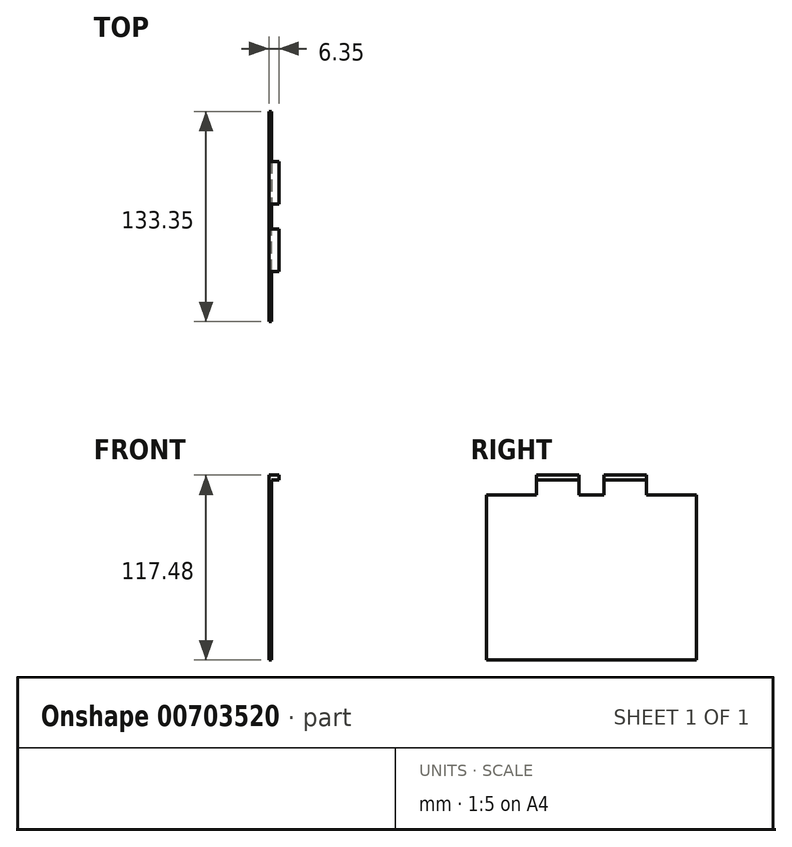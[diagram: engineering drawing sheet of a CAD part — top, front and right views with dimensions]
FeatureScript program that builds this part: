
annotation { "Feature Type Name" : "Feature", "Feature Type Description" : "" }
export const myFeature = defineFeature(function(context is Context, id is Id, definition is map)
    precondition{}
    {
        {
            var Q0;
            Q0=qCreatedBy(makeId("Front.planeOp"),FACE);
            var sketch = newSketch(context, id + "F0", { "sketchPlane" : qUnion([Q0])});
            skLineSegment(sketch, "E0.bottom", {"start": v(-4.86, 82.67) * mm, "end": v(-3.27, 82.67) * mm});
            skLineSegment(sketch, "E0.top", {"start": v(-4.86, -18.93) * mm, "end": v(-3.27, -18.93) * mm});
            skLineSegment(sketch, "E0.left", {"start": v(-4.86, 82.67) * mm, "end": v(-4.86, -18.93) * mm});
            skLineSegment(sketch, "E0.right", {"start": v(-3.27, 82.67) * mm, "end": v(-3.27, -18.93) * mm});
            skLineSegment(sketch, "E1.bottom", {"start": v(-4.86, 95.37) * mm, "end": v(-3.27, 95.37) * mm});
            skLineSegment(sketch, "E1.left", {"start": v(-4.86, 95.37) * mm, "end": v(-4.86, 82.67) * mm});
            skLineSegment(sketch, "E1.right", {"start": v(-3.27, 95.37) * mm, "end": v(-3.27, 82.67) * mm});
            skLineSegment(sketch, "E2.bottom", {"start": v(-4.86, 95.37) * mm, "end": v(1.5, 95.37) * mm});
            skLineSegment(sketch, "E2.top", {"start": v(-4.86, 98.55) * mm, "end": v(1.5, 98.55) * mm});
            skLineSegment(sketch, "E2.left", {"start": v(-4.86, 95.37) * mm, "end": v(-4.86, 98.55) * mm});
            skLineSegment(sketch, "E2.right", {"start": v(1.5, 95.37) * mm, "end": v(1.5, 98.55) * mm});
            skLineSegment(sketch, "E3.bottom", {"start": v(1.5, 95.37) * mm, "end": v(-0.1, 95.37) * mm});
            skLineSegment(sketch, "E3.top", {"start": v(1.5, 89.02) * mm, "end": v(-0.1, 89.02) * mm});
            skLineSegment(sketch, "E3.left", {"start": v(1.5, 95.37) * mm, "end": v(1.5, 89.02) * mm});
            skLineSegment(sketch, "E3.right", {"start": v(-0.1, 95.37) * mm, "end": v(-0.1, 89.02) * mm});
            skPoint(sketch, "E4", {"position": v(-4.86, 31.87) * mm});
            skSolve(sketch);
        }
        {
            var Q0;
            Q0=makeQuery(id+"F0.imprint","IMPRINT",FACE,{"disambiguationData":[TD([[makeQuery(id+"F0.imprint","IMPRINT",EDGE,{"derivedFrom":sQuery(id+"F0.wireOp",EDGE,"E2.top")}),-1.0]])]});
            var Q1;
            Q1=makeQuery(id+"F0.imprint","IMPRINT",FACE,{"disambiguationData":[TD([[makeQuery(id+"F0.imprint","IMPRINT",EDGE,{"derivedFrom":sQuery(id+"F0.wireOp",EDGE,"E0.bottom")}),1.0]])]});
            var Q2;
            Q2=makeQuery(id+"F0.imprint","IMPRINT",FACE,{"disambiguationData":[TD([[makeQuery(id+"F0.imprint","IMPRINT",EDGE,{"derivedFrom":sQuery(id+"F0.wireOp",EDGE,"E3.bottom")}),1.0]])]});
            var Q3;
            Q3=makeQuery(id+"F0.imprint","IMPRINT",FACE,{"disambiguationData":[TD([[makeQuery(id+"F0.imprint","IMPRINT",EDGE,{"derivedFrom":sQuery(id+"F0.wireOp",EDGE,"E0.top")}),1.0]])]});
            extrude(context, id + "F1", {"entities" : qUnion([Q0, Q1, Q2, Q3]), "depth" : 66.67 * mm, "hasOffset" : true, "offsetDistance" : 25.4 * mm, "hasDraft" : true, "draftAngle" : 0 * degree});
        }
        {
            var Q0;
            Q0=makeQuery(id+"F1.opExtrude","CAP_FACE",FACE,{"disambiguationData":[OSD([sQuery(id+"F0.wireOp",EDGE,"E0.top"),sQuery(id+"F0.wireOp",EDGE,"E0.left"),sQuery(id+"F0.wireOp",EDGE,"E0.right"),sQuery(id+"F0.wireOp",EDGE,"E1.left"),sQuery(id+"F0.wireOp",EDGE,"E1.right"),sQuery(id+"F0.wireOp",EDGE,"E2.bottom"),sQuery(id+"F0.wireOp",EDGE,"E2.top"),sQuery(id+"F0.wireOp",EDGE,"E2.left"),sQuery(id+"F0.wireOp",EDGE,"E2.right"),sQuery(id+"F0.wireOp",EDGE,"E3.top"),sQuery(id+"F0.wireOp",EDGE,"E3.left"),sQuery(id+"F0.wireOp",EDGE,"E3.right")])],"isStart":false});
            var sketch = newSketch(context, id + "F2", { "sketchPlane" : qUnion([Q0])});
            skLineSegment(sketch, "E5", {"start": v(-4.86, 85.88) * mm, "end": v(-3.27, 85.88) * mm});
            skSolve(sketch);
        }
        {
            var Q0;
            {var subQ2=sQuery(id+"F2.wireOp",EDGE,"E5");Q0=makeQuery(id+"F2.imprint","IMPRINT",FACE,{"disambiguationData":[TD([[makeQuery(id+"F2.imprint","IMPRINT",EDGE,{"derivedFrom":subQ2}),1.0]])]});}
            extrude(context, id + "F3", {"entities" : qUnion([Q0]), "operationType" : NewBodyOperationType.REMOVE, "oppositeDirection" : true, "depth" : 7.94 * mm, "offsetDistance" : 25.4 * mm});
        }
        {
            var Q0;
            Q0=makeQuery(id+"F1.opExtrude","CAP_FACE",FACE,{"disambiguationData":[OSD([sQuery(id+"F0.wireOp",EDGE,"E0.top"),sQuery(id+"F0.wireOp",EDGE,"E0.left"),sQuery(id+"F0.wireOp",EDGE,"E0.right"),sQuery(id+"F0.wireOp",EDGE,"E1.left"),sQuery(id+"F0.wireOp",EDGE,"E1.right"),sQuery(id+"F0.wireOp",EDGE,"E2.bottom"),sQuery(id+"F0.wireOp",EDGE,"E2.top"),sQuery(id+"F0.wireOp",EDGE,"E2.left"),sQuery(id+"F0.wireOp",EDGE,"E2.right"),sQuery(id+"F0.wireOp",EDGE,"E3.top"),sQuery(id+"F0.wireOp",EDGE,"E3.left"),sQuery(id+"F0.wireOp",EDGE,"E3.right")])],"isStart":true});
            var sketch = newSketch(context, id + "F4", { "sketchPlane" : qUnion([Q0])});
            skLineSegment(sketch, "E6", {"start": v(4.86, 85.86) * mm, "end": v(3.27, 85.86) * mm});
            skSolve(sketch);
        }
        {
            var Q0;
            {var subQ2=sQuery(id+"F4.wireOp",EDGE,"E6");Q0=makeQuery(id+"F4.imprint","IMPRINT",FACE,{"disambiguationData":[TD([[makeQuery(id+"F4.imprint","IMPRINT",EDGE,{"derivedFrom":subQ2}),-1.0]])]});}
            extrude(context, id + "F5", {"entities" : qUnion([Q0]), "operationType" : NewBodyOperationType.REMOVE, "oppositeDirection" : true, "depth" : 31.75 * mm, "offsetDistance" : 25.4 * mm});
        }
        {
            var Q0;
            Q0=makeQuery(id+"F1.opExtrude","SWEPT_BODY",BODY,{"disambiguationData":[OSD([sQuery(id+"F0.wireOp",EDGE,"E0.top"),sQuery(id+"F0.wireOp",EDGE,"E0.left"),sQuery(id+"F0.wireOp",EDGE,"E0.right"),sQuery(id+"F0.wireOp",EDGE,"E1.left"),sQuery(id+"F0.wireOp",EDGE,"E1.right"),sQuery(id+"F0.wireOp",EDGE,"E2.bottom"),sQuery(id+"F0.wireOp",EDGE,"E2.top"),sQuery(id+"F0.wireOp",EDGE,"E2.left"),sQuery(id+"F0.wireOp",EDGE,"E2.right"),sQuery(id+"F0.wireOp",EDGE,"E3.top"),sQuery(id+"F0.wireOp",EDGE,"E3.left"),sQuery(id+"F0.wireOp",EDGE,"E3.right")])]});
            var Q1;
            Q1=makeQuery(id+"F1.opExtrude","CAP_FACE",FACE,{"disambiguationData":[OSD([sQuery(id+"F0.wireOp",EDGE,"E0.top"),sQuery(id+"F0.wireOp",EDGE,"E0.left"),sQuery(id+"F0.wireOp",EDGE,"E0.right"),sQuery(id+"F0.wireOp",EDGE,"E1.left"),sQuery(id+"F0.wireOp",EDGE,"E1.right"),sQuery(id+"F0.wireOp",EDGE,"E2.bottom"),sQuery(id+"F0.wireOp",EDGE,"E2.top"),sQuery(id+"F0.wireOp",EDGE,"E2.left"),sQuery(id+"F0.wireOp",EDGE,"E2.right"),sQuery(id+"F0.wireOp",EDGE,"E3.top"),sQuery(id+"F0.wireOp",EDGE,"E3.left"),sQuery(id+"F0.wireOp",EDGE,"E3.right")])],"isStart":false});
            mirror(context, id + "F6", {"operationType" : NewBodyOperationType.ADD, "entities" : qUnion([Q0]), "mirrorPlane" : qUnion([Q1])});
        }
    });
